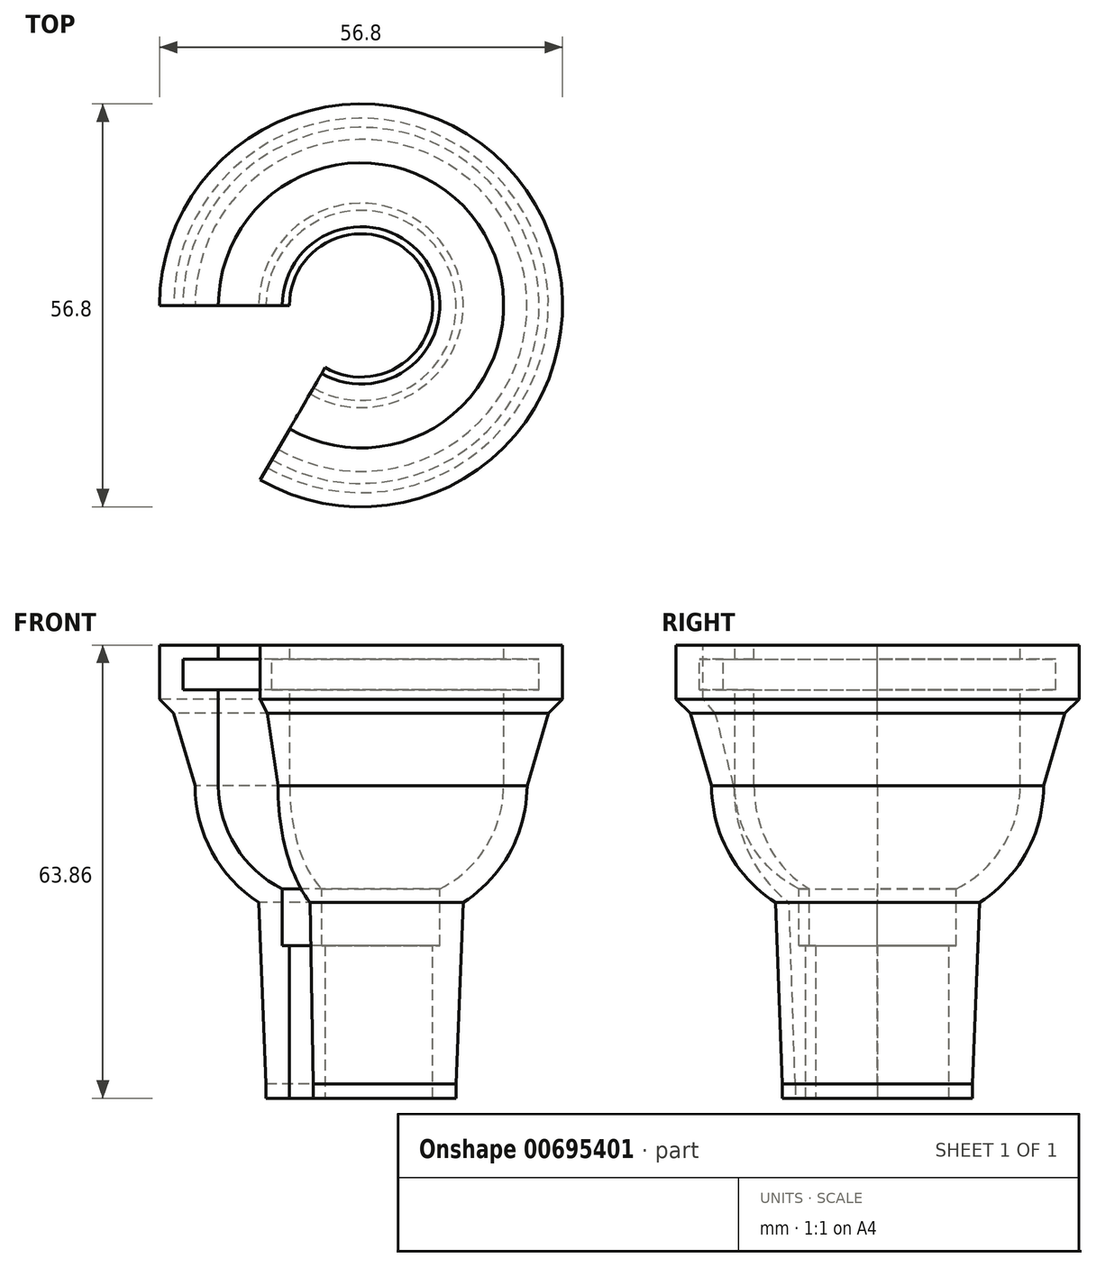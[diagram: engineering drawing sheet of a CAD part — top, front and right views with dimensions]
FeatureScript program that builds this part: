
annotation { "Feature Type Name" : "Feature", "Feature Type Description" : "" }
export const myFeature = defineFeature(function(context is Context, id is Id, definition is map)
    precondition{}
    {
        {
            var Q0;
            Q0=qCreatedBy(makeId("Front.planeOp"),FACE);
            var sketch = newSketch(context, id + "F0", { "sketchPlane" : qUnion([Q0])});
            skLineSegment(sketch, "E0", {"start": v(-10.1, -49.4) * mm, "end": v(-10.1, -31.19) * mm});
            skLineSegment(sketch, "E1", {"start": v(-10.1, -31.19) * mm, "end": v(-11.1, -31.19) * mm});
            skLineSegment(sketch, "E2", {"start": v(-11.1, -31.19) * mm, "end": v(-11.1, -23.19) * mm});
            skLineSegment(sketch, "E3", {"start": v(-11.1, -23.19) * mm, "end": v(-11.1, -8.69) * mm, "construction": true});
            skLineSegment(sketch, "E4", {"start": v(0, -8.64) * mm, "end": v(-19.15, -8.64) * mm, "construction": true});
            skLineSegment(sketch, "E5", {"start": v(-19.15, -8.64) * mm, "end": v(-20.1, -8.64) * mm});
            skLineSegment(sketch, "E6", {"start": v(-20.1, -8.64) * mm, "end": v(-20.1, 4.86) * mm});
            skLineSegment(sketch, "E7", {"start": v(-20.1, 4.86) * mm, "end": v(-25.1, 4.86) * mm});
            skArc(sketch, "E8", {"start": v(-20.1, -8.64) * mm, "mid": v(-17.67, -17.2) * mm, "end": v(-11.1, -23.19) * mm});
            skLineSegment(sketch, "E9.1", {"start": v(-28.4, 3.56) * mm, "end": v(-28.4, 9.16) * mm});
            skArc(sketch, "E9.4", {"start": v(-23.4, -8.64) * mm, "mid": v(-21, -18.02) * mm, "end": v(-14.4, -25.1) * mm});
            skPoint(sketch, "E10.visualSharp", {"position": v(-28.4, 1.56) * mm});
            skLineSegment(sketch, "E11", {"start": v(-13.4, -50.7) * mm, "end": v(-14.4, -25.1) * mm});
            skLineSegment(sketch, "E12", {"start": v(-10.1, -49.4) * mm, "end": v(-10.1, -52.7) * mm});
            skLineSegment(sketch, "E13", {"start": v(-11.4, -52.7) * mm, "end": v(-10.1, -52.7) * mm});
            skLineSegment(sketch, "E14", {"start": v(0, 9.68) * mm, "end": v(0, -52.91) * mm, "construction": true});
            skLineSegment(sketch, "E15", {"start": v(-23.4, -8.64) * mm, "end": v(-26.4, 1.56) * mm});
            skLineSegment(sketch, "E16", {"start": v(-26.4, 1.56) * mm, "end": v(-28.4, 3.56) * mm});
            skLineSegment(sketch, "E17", {"start": v(-28.4, 9.16) * mm, "end": v(-28.4, 11.16) * mm});
            skLineSegment(sketch, "E18", {"start": v(-28.4, 11.16) * mm, "end": v(-20.1, 11.16) * mm});
            skLineSegment(sketch, "E19", {"start": v(-25.1, 4.86) * mm, "end": v(-25.1, 9.16) * mm});
            skLineSegment(sketch, "E20", {"start": v(-25.1, 9.16) * mm, "end": v(-20.1, 9.16) * mm});
            skLineSegment(sketch, "E21", {"start": v(-20.1, 9.16) * mm, "end": v(-20.1, 11.16) * mm});
            skLineSegment(sketch, "E22", {"start": v(-13.4, -50.7) * mm, "end": v(-13.4, -52.7) * mm});
            skLineSegment(sketch, "E23", {"start": v(-13.4, -52.7) * mm, "end": v(-11.4, -52.7) * mm});
            skSolve(sketch);
        }
        {
            var Q0;
            Q0 = qSketchRegion(id + "F0", true);
            var Q1;
            Q1=sQuery(id+"F0.wireOp",EDGE,"E14");
            revolve(context, id + "F1", {"entities" : qUnion([Q0]), "axis" : qUnion([Q1]), "revolveType" : RevolveType.ONE_DIRECTION, "angle" : 300 * degree, "surfaceOperationType" : NewSurfaceOperationType.NEW});
        }
    });
